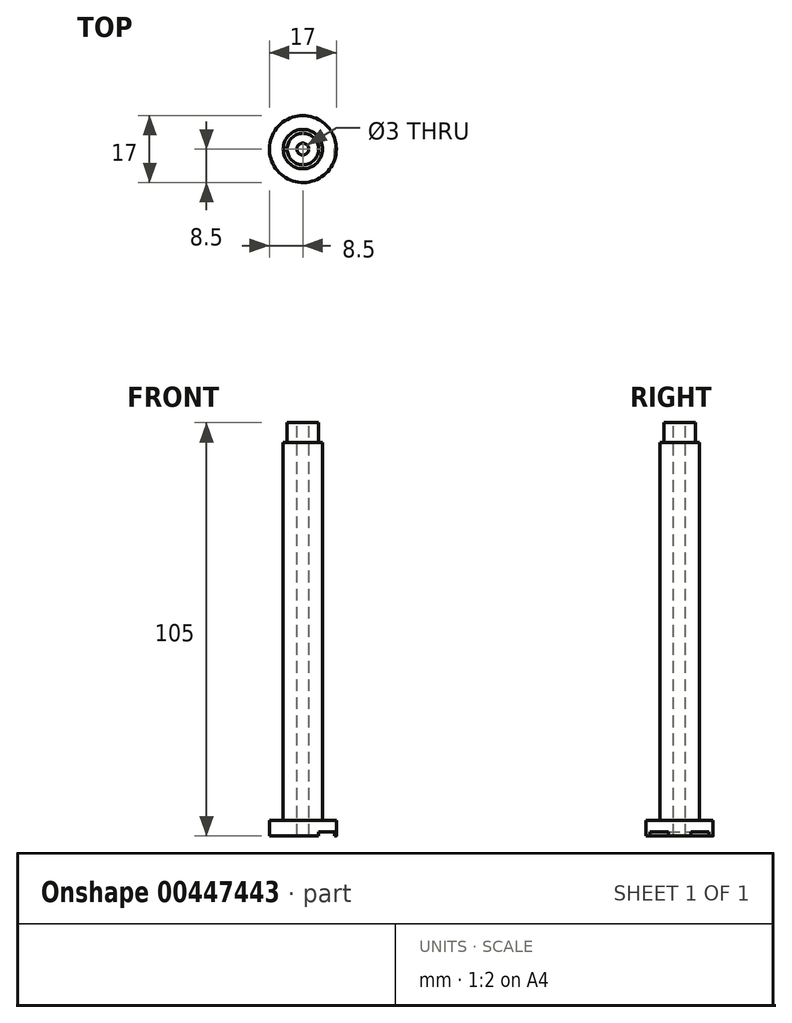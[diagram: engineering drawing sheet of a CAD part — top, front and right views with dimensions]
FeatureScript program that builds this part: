
annotation { "Feature Type Name" : "Feature", "Feature Type Description" : "" }
export const myFeature = defineFeature(function(context is Context, id is Id, definition is map)
    precondition{}
    {
        {
            var Q0;
            Q0=qCreatedBy(makeId("Top.planeOp"),FACE);
            var sketch = newSketch(context, id + "F0", { "sketchPlane" : qUnion([Q0])});
            skCircle(sketch, "E0", {"center": v(0, 0) * mm, "radius": 8.5 * mm});
            skSolve(sketch);
        }
        {
            var Q0;
            Q0=qSketchRegion(id+"F0",true);
            extrude(context, id + "F1", {"entities" : qUnion([Q0]), "depth" : 4 * mm});
        }
        {
            var Q0;
            Q0=qCreatedBy(makeId("Top.planeOp"),FACE);
            var sketch = newSketch(context, id + "F2", { "sketchPlane" : qUnion([Q0])});
            skCircle(sketch, "E1", {"center": v(0, 0) * mm, "radius": 5 * mm});
            skSolve(sketch);
        }
        {
            var Q0;
            Q0=qSketchRegion(id+"F2",true);
            extrude(context, id + "F3", {"entities" : qUnion([Q0]), "operationType" : NewBodyOperationType.ADD, "depth" : 100 * mm});
        }
        {
            var Q0;
            Q0=qCreatedBy(makeId("Right.planeOp"),FACE);
            var sketch = newSketch(context, id + "F4", { "sketchPlane" : qUnion([Q0])});
            skLineSegment(sketch, "E2.bottom", {"start": v(0, 105) * mm, "end": v(4, 105) * mm});
            skLineSegment(sketch, "E2.top", {"start": v(0, 100) * mm, "end": v(4, 100) * mm});
            skLineSegment(sketch, "E2.left", {"start": v(0, 105) * mm, "end": v(0, 100) * mm});
            skLineSegment(sketch, "E2.right", {"start": v(4, 105) * mm, "end": v(4, 100) * mm});
            skSolve(sketch);
        }
        {
            var Q0;
            Q0=makeQuery(id+"F4.imprint","IMPRINT",FACE,{"disambiguationData":[TD([[makeQuery(id+"F4.imprint","IMPRINT",EDGE,{"derivedFrom":sQuery(id+"F4.wireOp",EDGE,"E2.bottom")}),-1.0]])]});
            var Q1;
            Q1=sQuery(id+"F4.wireOp",EDGE,"E2.left");
            revolve(context, id + "F5", {"operationType" : NewBodyOperationType.ADD, "entities" : qUnion([Q0]), "axis" : qUnion([Q1]), "revolveType" : RevolveType.FULL});
        }
        {
            var Q0;
            Q0=makeQuery(id+"F1.opExtrude","CAP_FACE",FACE,{"disambiguationData":[OSD([sQuery(id+"F0.wireOp",EDGE,"E0")])],"isStart":true});
            var sketch = newSketch(context, id + "F6", { "sketchPlane" : qUnion([Q0])});
            skLineSegment(sketch, "E3.bottom", {"start": v(4, 17.7) * mm, "end": v(8, 17.7) * mm});
            skLineSegment(sketch, "E3.top", {"start": v(4, -19.2) * mm, "end": v(8, -19.2) * mm});
            skLineSegment(sketch, "E3.left", {"start": v(4, 17.7) * mm, "end": v(4, -19.2) * mm});
            skLineSegment(sketch, "E3.right", {"start": v(8, 17.7) * mm, "end": v(8, -19.2) * mm});
            skSolve(sketch);
        }
        {
            var Q0;
            Q0=qSketchRegion(id+"F6",true);
            extrude(context, id + "F7", {"entities" : qUnion([Q0]), "operationType" : NewBodyOperationType.REMOVE, "oppositeDirection" : true, "depth" : 1 * mm});
        }
        {
            var Q0;
            Q0=makeQuery(id+"F5.opRevolve","SWEPT_FACE",FACE,{"disambiguationData":[OSD([sQuery(id+"F4.wireOp",EDGE,"E2.bottom")])]});
            var sketch = newSketch(context, id + "F8", { "sketchPlane" : qUnion([Q0])});
            skCircle(sketch, "E4", {"center": v(0, 0) * mm, "radius": 1.5 * mm});
            skSolve(sketch);
        }
        {
            var Q0;
            Q0 = qSketchRegion(id + "F8", true);
            extrude(context, id + "F9", {"entities" : qUnion([Q0]), "operationType" : NewBodyOperationType.REMOVE, "oppositeDirection" : true, "depth" : 122 * mm});
        }
    });
